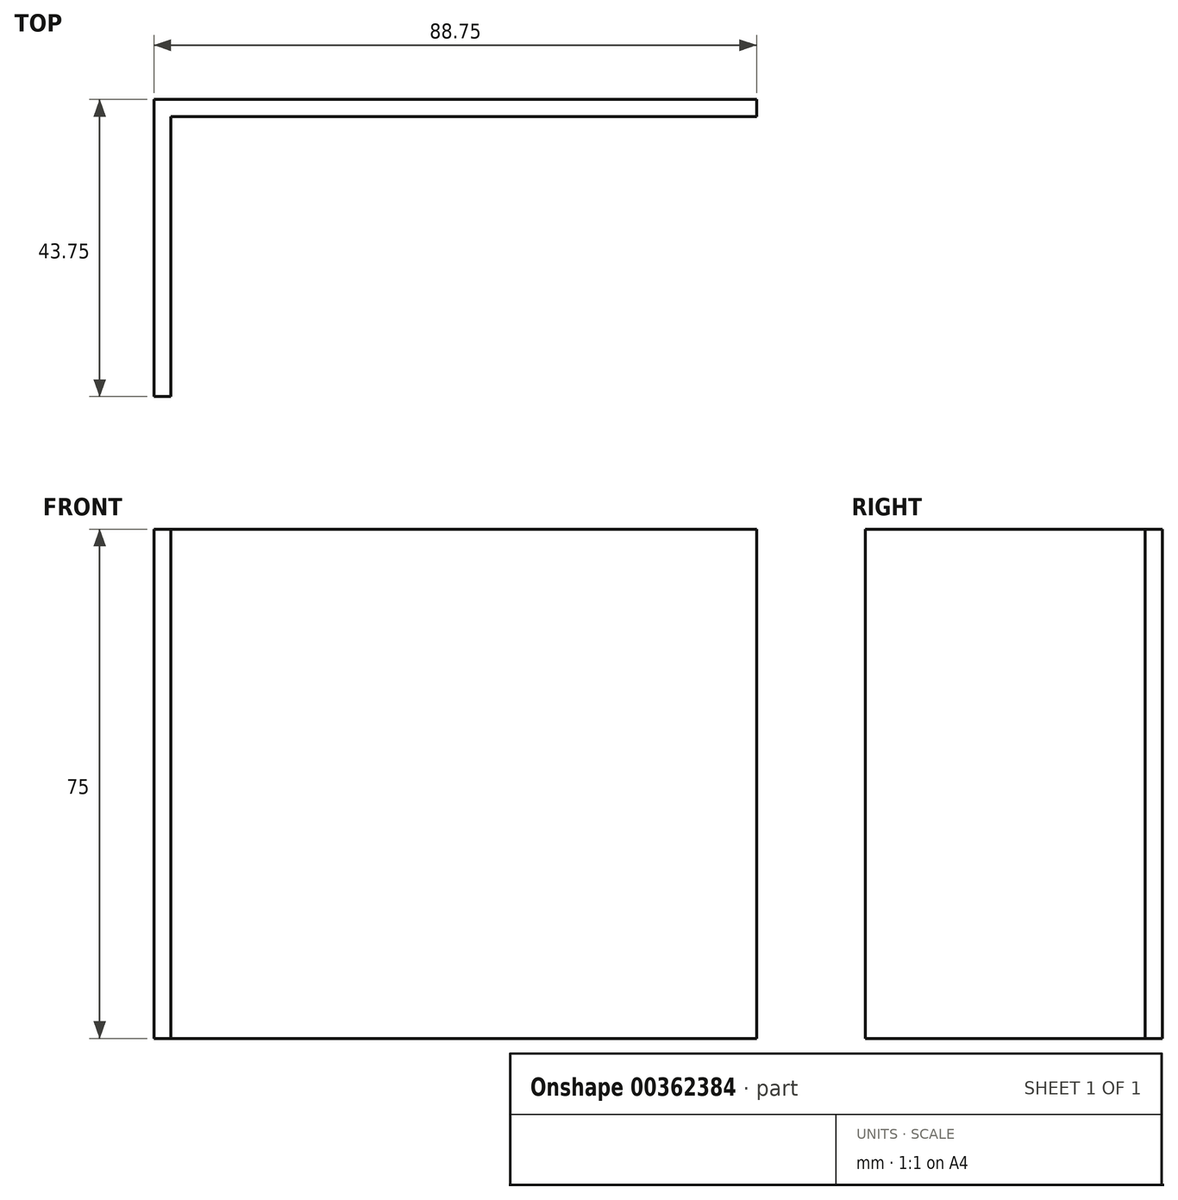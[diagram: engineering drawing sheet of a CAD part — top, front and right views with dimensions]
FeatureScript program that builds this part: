
annotation { "Feature Type Name" : "Feature", "Feature Type Description" : "" }
export const myFeature = defineFeature(function(context is Context, id is Id, definition is map)
    precondition{}
    {
        {
            var Q0;
            Q0=qCreatedBy(makeId("Top.planeOp"),FACE);
            var sketch = newSketch(context, id + "F0", { "sketchPlane" : qUnion([Q0])});
            skLineSegment(sketch, "E0", {"start": v(-42.5, -45.88) * mm, "end": v(-42.5, -2.13) * mm});
            skLineSegment(sketch, "E1", {"start": v(-42.5, -2.13) * mm, "end": v(46.25, -2.13) * mm});
            skLineSegment(sketch, "E2", {"start": v(46.25, -2.13) * mm, "end": v(46.25, -4.63) * mm});
            skLineSegment(sketch, "E3", {"start": v(46.25, -4.63) * mm, "end": v(-40, -4.63) * mm});
            skLineSegment(sketch, "E4", {"start": v(-40, -4.63) * mm, "end": v(-40, -45.88) * mm});
            skLineSegment(sketch, "E5", {"start": v(-40, -45.88) * mm, "end": v(-42.5, -45.88) * mm});
            skSolve(sketch);
        }
        {
            var Q0;
            Q0=makeQuery(id+"F0.imprint","IMPRINT",FACE,{"disambiguationData":[TD([[makeQuery(id+"F0.imprint","IMPRINT",EDGE,{"derivedFrom":sQuery(id+"F0.wireOp",EDGE,"E0")}),-1.0]])]});
            extrude(context, id + "F1", {"entities" : qUnion([Q0]), "depth" : 75 * mm});
        }
    });
